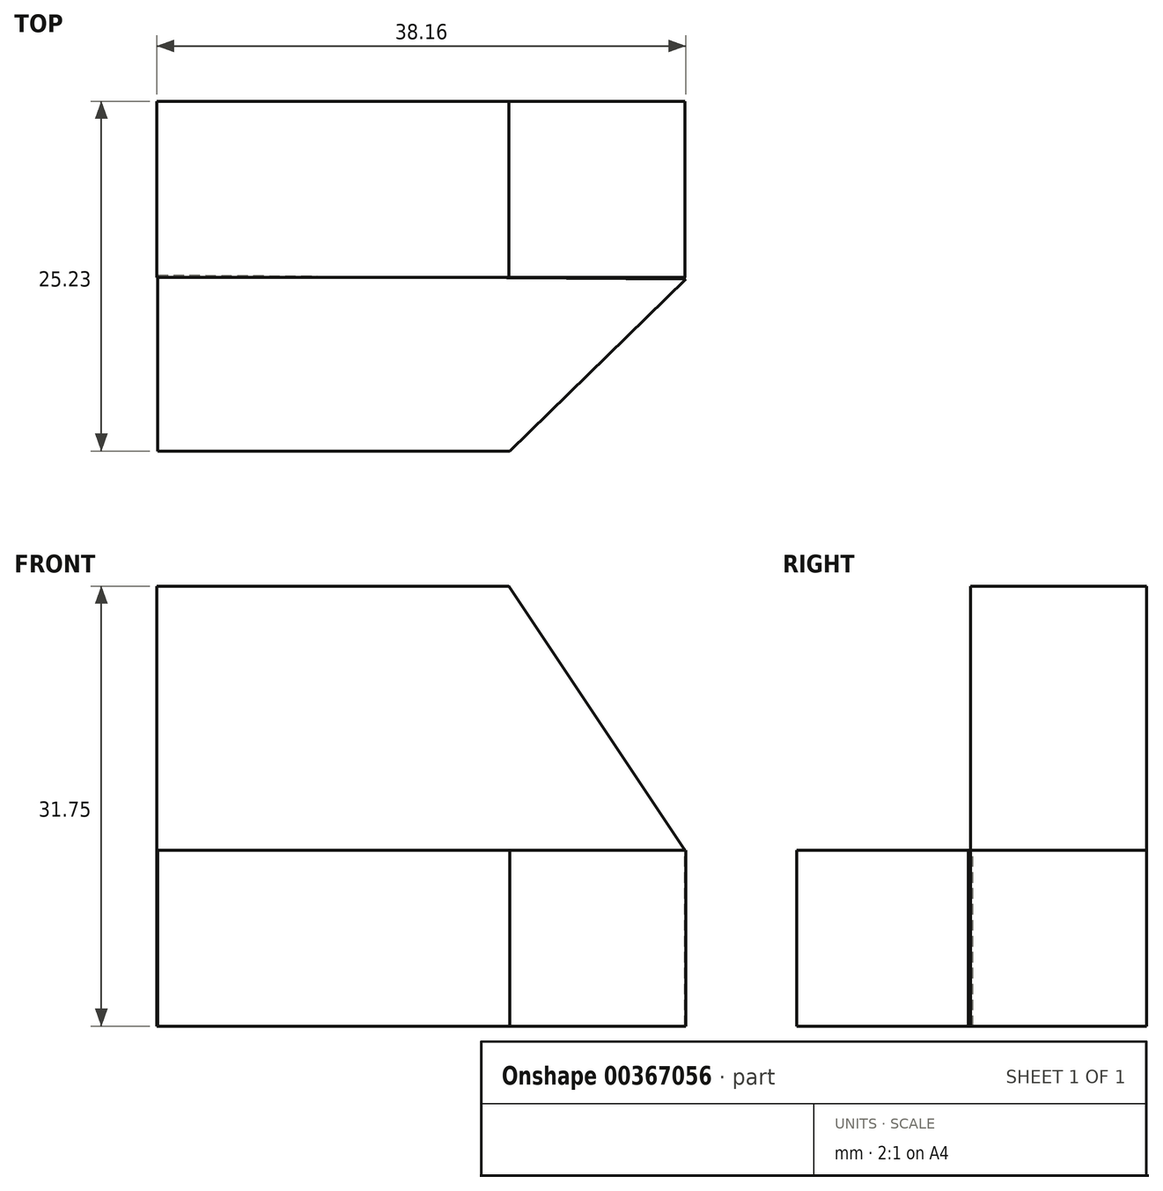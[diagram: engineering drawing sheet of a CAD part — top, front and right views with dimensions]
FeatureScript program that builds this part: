
annotation { "Feature Type Name" : "Feature", "Feature Type Description" : "" }
export const myFeature = defineFeature(function(context is Context, id is Id, definition is map)
    precondition{}
    {
        {
            var Q0;
            Q0=qCreatedBy(makeId("Front.planeOp"),FACE);
            var sketch = newSketch(context, id + "F0", { "sketchPlane" : qUnion([Q0])});
            skLineSegment(sketch, "E0", {"start": v(-12.43, 0) * mm, "end": v(-50.53, 0) * mm});
            skLineSegment(sketch, "E1", {"start": v(-50.53, 0) * mm, "end": v(-50.53, 19.05) * mm});
            skLineSegment(sketch, "E2", {"start": v(-50.53, 19.05) * mm, "end": v(-25.13, 19.05) * mm});
            skLineSegment(sketch, "E3", {"start": v(-25.13, 19.05) * mm, "end": v(-12.43, 0) * mm});
            skLineSegment(sketch, "E4", {"start": v(-50.53, 0) * mm, "end": v(-50.53, -12.7) * mm});
            skLineSegment(sketch, "E5", {"start": v(-50.53, -12.7) * mm, "end": v(-12.43, -12.7) * mm});
            skLineSegment(sketch, "E6", {"start": v(-12.43, -12.7) * mm, "end": v(-12.43, 0) * mm});
            skSolve(sketch);
        }
        {
            var Q0;
            Q0=makeQuery(id+"F0.imprint","IMPRINT",FACE,{"disambiguationData":[TD([[makeQuery(id+"F0.imprint","IMPRINT",EDGE,{"derivedFrom":sQuery(id+"F0.wireOp",EDGE,"E0")}),-1.0]])]});
            var Q1;
            Q1=makeQuery(id+"F0.imprint","IMPRINT",FACE,{"disambiguationData":[TD([[makeQuery(id+"F0.imprint","IMPRINT",EDGE,{"derivedFrom":sQuery(id+"F0.wireOp",EDGE,"E0")}),1.0]])]});
            extrude(context, id + "F1", {"entities" : qUnion([Q0, Q1]), "depth" : 12.7 * mm});
        }
        {
            var Q0;
            Q0=qCreatedBy(makeId("Top.planeOp"),FACE);
            var sketch = newSketch(context, id + "F2", { "sketchPlane" : qUnion([Q0])});
            skLineSegment(sketch, "E7", {"start": v(-50.47, -12.53) * mm, "end": v(-50.47, -25.23) * mm});
            skLineSegment(sketch, "E8", {"start": v(-50.47, -25.23) * mm, "end": v(-25.07, -25.23) * mm});
            skLineSegment(sketch, "E9", {"start": v(-25.07, -25.23) * mm, "end": v(-12.37, -12.84) * mm});
            skLineSegment(sketch, "E10", {"start": v(-50.47, -12.53) * mm, "end": v(-12.37, -12.84) * mm});
            skSolve(sketch);
        }
        {
            var Q0;
            Q0=makeQuery(id+"F2.imprint","IMPRINT",FACE,{"disambiguationData":[TD([[makeQuery(id+"F2.imprint","IMPRINT",EDGE,{"derivedFrom":sQuery(id+"F2.wireOp",EDGE,"E7")}),1.0]])]});
            extrude(context, id + "F3", {"entities" : qUnion([Q0]), "oppositeDirection" : true, "depth" : 12.7 * mm});
        }
    });
